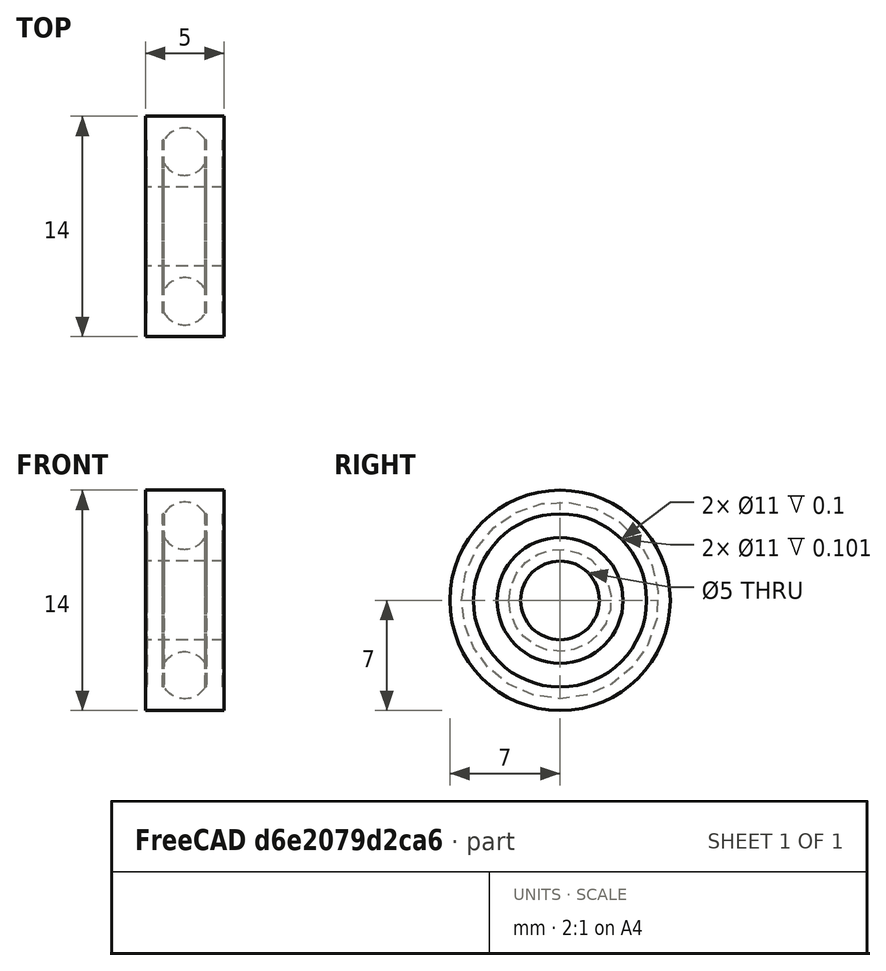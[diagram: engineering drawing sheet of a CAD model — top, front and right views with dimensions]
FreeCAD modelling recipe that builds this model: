
FCSTD DOCUMENT  (FreeCAD 0.21R38887 (Git))
Label: подшипник
License: All rights reserved
LicenseURL: http://en.wikipedia.org/wiki/All_rights_reserved
objects: Sketcher::SketchObject×1, PartDesign::Revolution×1, PartDesign::Body×1
note: 6 computed .brp shape members not serialized (recipe doc carries the construction recipe); baked Part::Feature solids carry a one-line shape summary decoded from their .brp
EXTERNAL_REF file=ТаблицаПараметров.FCStd obj=Spreadsheet002

FEATURE [Sketcher::SketchObject] Sketch
  ArcFitTolerance = 0
  AttachmentSupport = -> [YZ_Plane]
  ExternalBSplineMaxDegree = 0
  ExternalBSplineTolerance = 0
  FullyConstrained = true
  InternalTolerance = 1e-06
  InvalidShape = false
  MakeInternals = false
  MapMode = 3
  Placement = pos=(0,0,0) rot=(0.707107,0.707107,0;3.14159rad)
  Support = -> [YZ_Plane]
  TreeRank = 0
  ValidateShape = false
  expr: Constraints[17] = <<ТаблицаПараметров>>#<<Ролик>>.diamPodsh / 2
  expr: Constraints[18] = <<ТаблицаПараметров>>#<<Ролик>>.dimD2 / 2
  expr: Constraints[19] = ТаблицаПараметров#<<Ролик>>.dimH1
  expr: Constraints[21] = (<<ТаблицаПараметров>>#<<Ролик>>.dimD2 / 2 - <<ТаблицаПараметров>>#<<Ролик>>.diamPodsh / 2) / 3
  expr: Constraints[22] = (<<ТаблицаПараметров>>#<<Ролик>>.dimD2 / 2 - <<ТаблицаПараметров>>#<<Ролик>>.diamPodsh / 2) / 3 * 2
  expr: Constraints[23] = -((<<ТаблицаПараметров>>#<<Ролик>>.dimD2 / 2 - <<ТаблицаПараметров>>#<<Ролик>>.diamPodsh / 2) / 2 + <<ТаблицаПараметров>>#<<Ролик>>.diamPodsh / 2)
  sketch-geometry (20):
    g0: LineSegment StartX=-7 StartY=2.5 StartZ=0 EndX=-5.5 EndY=2.5 EndZ=0
    g1: LineSegment StartX=-5.5 StartY=2.5 StartZ=0 EndX=-5.5 EndY=2.4 EndZ=0
    g2: LineSegment StartX=-5.5 StartY=-2.5 StartZ=0 EndX=-7 EndY=-2.5 EndZ=0
    g3: LineSegment StartX=-7 StartY=-2.5 StartZ=0 EndX=-7 EndY=2.5 EndZ=0
    g4: LineSegment StartX=-4 StartY=2.5 StartZ=0 EndX=-2.5 EndY=2.5 EndZ=0
    g5: LineSegment StartX=-2.5 StartY=2.5 StartZ=0 EndX=-2.5 EndY=-2.5 EndZ=0
    g6: LineSegment StartX=-2.5 StartY=-2.5 StartZ=0 EndX=-4 EndY=-2.5 EndZ=0
    g7: LineSegment StartX=-4 StartY=-2.5 StartZ=0 EndX=-4 EndY=-2.4 EndZ=0
    g8: ArcOfCircle CenterX=-4.75 CenterY=-1e-16 CenterZ=0 NormalX=0 NormalY=0 NormalZ=1 AngleXU=0 Radius=1.5 StartAngle=2.0944 EndAngle=4.18879
    g9: LineSegment StartX=-5.5 StartY=-1.29904 StartZ=0 EndX=-5.5 EndY=-1.4 EndZ=0
    g10: LineSegment StartX=-4 StartY=1.29904 StartZ=0 EndX=-4 EndY=1.4 EndZ=0
    g11: ArcOfCircle CenterX=-4.75 CenterY=-1e-16 CenterZ=0 NormalX=0 NormalY=0 NormalZ=1 AngleXU=0 Radius=1.5 StartAngle=5.23599 EndAngle=7.33038
    g12: LineSegment StartX=-5.5 StartY=2.4 StartZ=0 EndX=-4 EndY=2.4 EndZ=0
    g13: LineSegment StartX=-5.5 StartY=1.4 StartZ=0 EndX=-4 EndY=1.4 EndZ=0
    g14: LineSegment StartX=-5.5 StartY=-2.4 StartZ=0 EndX=-4 EndY=-2.4 EndZ=0
    g15: LineSegment StartX=-4 StartY=-1.4 StartZ=0 EndX=-5.5 EndY=-1.4 EndZ=0
    g16: LineSegment StartX=-5.5 StartY=1.4 StartZ=0 EndX=-5.5 EndY=1.29904 EndZ=0
    g17: LineSegment StartX=-4 StartY=2.4 StartZ=0 EndX=-4 EndY=2.5 EndZ=0
    g18: LineSegment StartX=-5.5 StartY=-2.4 StartZ=0 EndX=-5.5 EndY=-2.5 EndZ=0
    g19: LineSegment StartX=-4 StartY=-1.4 StartZ=0 EndX=-4 EndY=-1.29904 EndZ=0
  constraints (59):
    c: Coincident(g0,g1)
    c: Coincident(g18,g2)
    c: Coincident(g2,g3)
    c: Coincident(g3,g0)
    c: Horizontal(g0)
    c: Horizontal(g2)
    c: Vertical(g1)
    c: Symmetric(g0,g2,g-1)
    c: Coincident(g4,g5)
    c: Coincident(g5,g6)
    c: Coincident(g6,g7)
    c: Coincident(g17,g4)
    c: Horizontal(g4)
    c: Horizontal(g6)
    c: Vertical(g7)
    c: Symmetric(g4,g5,g-1)
    c: Equal(g3,g5)
    c: DistanceX(g5,g-1) = 2.5
    c: DistanceX(g2,g-1) = 7
    c: DistanceY(g3,g3) = 5
    c: Equal(g4,g0)
    c: DistanceX(g4,g4) = 1.5
    c: Diameter(g8) = 3
    c: DistanceX(g8) = -4.75
    c: Coincident(g11,g10)
    c: Coincident(g8,g16)
    c: Equal(g8,g11)
    c: Coincident(g8,g9)
    c: Coincident(g11,g19)
    c: Coincident(g8,g11)
    c: Vertical(g9)
    c: Equal(g2,g0)
    c: Horizontal(g12)
    c: Horizontal(g13)
    c: Horizontal(g14)
    c: Horizontal(g15)
    c: Coincident(g1,g12)
    c: Coincident(g16,g13)
    c: Coincident(g10,g13)
    c: Coincident(g17,g12)
    c: DistanceY(g1,g1) = 0.1
    c: DistanceY(g13,g1) = 1
    c: Coincident(g9,g15)
    c: Coincident(g18,g14)
    c: Coincident(g7,g14)
    c: Coincident(g19,g15)
    c: DistanceY(g18,g18) = 0.1
    c: DistanceY(g14,g9) = 1
    c: Equal(g4,g12)
    c: Equal(g13,g12)
    c: Equal(g12,g15)
    c: Equal(g15,g14)
    c: Equal(g10,g16)
    c: Equal(g16,g9)
    c: Equal(g9,g19)
    c: Vertical(g10)
    c: Vertical(g16)
    c: Vertical(g19)
    c: Equal(g14,g6)
FEATURE [PartDesign::Revolution] Revolution
  AddSubType = 0
  Angle = 360
  Axis = (1,0,0)
  Base = (0,0,0)
  ClaimChildren = false
  Fit = 0
  FitJoin = 0
  InnerFit = 0
  InnerFitJoin = 0
  InvalidShape = false
  NewSolid = false
  Placement = pos=(0,0,0) rot=(0.57735,0.57735,0.57735;2.0944rad)
  Profile = -> Sketch
  ReferenceAxis = -> X_Axis
  Suppress = false
  TreeRank = 0
  ValidateShape = true
  _ProfileBasedVersion = 0
FEATURE [PartDesign::Body] Body  label="Подшипник"
  AutoGroupSolids = false
  ClaimAllChildren = false
  ExportMode = 0
  Group = -> [Sketch,Revolution]
  InvalidShape = false
  Origin = -> Origin
  Tip = -> Revolution
  TreeRank = 2
  ValidateShape = false
  _ExportChildren = -> [Revolution]
  _GroupVersion = 1
